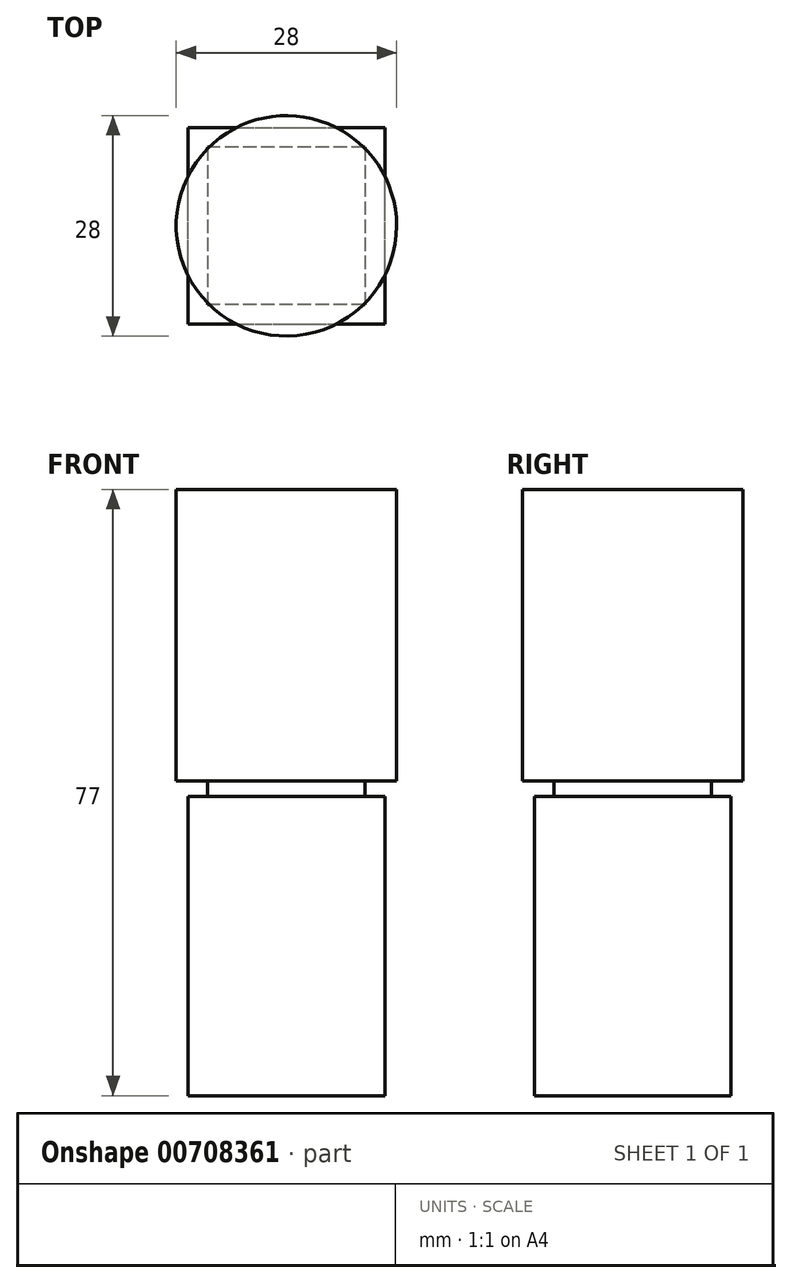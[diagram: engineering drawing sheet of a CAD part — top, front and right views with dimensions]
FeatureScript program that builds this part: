
annotation { "Feature Type Name" : "Feature", "Feature Type Description" : "" }
export const myFeature = defineFeature(function(context is Context, id is Id, definition is map)
    precondition{}
    {
        {
            var Q0;
            Q0=qCreatedBy(makeId("Top.planeOp"),FACE);
            var sketch = newSketch(context, id + "F0", { "sketchPlane" : qUnion([Q0])});
            skLineSegment(sketch, "E0.bottom", {"start": v(0, 0) * mm, "end": v(25, 0) * mm});
            skLineSegment(sketch, "E0.top", {"start": v(0, 25) * mm, "end": v(25, 25) * mm});
            skLineSegment(sketch, "E0.left", {"start": v(0, 0) * mm, "end": v(0, 25) * mm});
            skLineSegment(sketch, "E0.right", {"start": v(25, 0) * mm, "end": v(25, 25) * mm});
            skSolve(sketch);
        }
        {
            var Q0;
            Q0=makeQuery(id+"F0.imprint","IMPRINT",FACE,{"disambiguationData":[TD([[makeQuery(id+"F0.imprint","IMPRINT",EDGE,{"derivedFrom":sQuery(id+"F0.wireOp",EDGE,"E0.bottom")}),1.0]])]});
            extrude(context, id + "F1", {"entities" : qUnion([Q0]), "depth" : 38 * mm, "offsetDistance" : 25 * mm});
        }
        {
            var Q0;
            Q0=makeQuery(id+"F1.opExtrude","CAP_FACE",FACE,{"disambiguationData":[OSD([sQuery(id+"F0.wireOp",EDGE,"E0.bottom"),sQuery(id+"F0.wireOp",EDGE,"E0.top"),sQuery(id+"F0.wireOp",EDGE,"E0.left"),sQuery(id+"F0.wireOp",EDGE,"E0.right")])],"isStart":false});
            var sketch = newSketch(context, id + "F2", { "sketchPlane" : qUnion([Q0])});
            skPoint(sketch, "E1.centerSnap0", {"position": v(0, 12.5) * mm});
            skPoint(sketch, "E1.centerSnap1", {"position": v(12.5, 0) * mm});
            skLineSegment(sketch, "E2.bottom", {"start": v(22.5, 22.5) * mm, "end": v(2.5, 22.5) * mm});
            skLineSegment(sketch, "E2.top", {"start": v(22.5, 2.5) * mm, "end": v(2.5, 2.5) * mm});
            skLineSegment(sketch, "E2.left", {"start": v(22.5, 22.5) * mm, "end": v(22.5, 2.5) * mm});
            skLineSegment(sketch, "E2.right", {"start": v(2.5, 22.5) * mm, "end": v(2.5, 2.5) * mm});
            skPoint(sketch, "E2.middle", {"position": v(12.5, 12.5) * mm});
            skSolve(sketch);
        }
        {
            var Q0;
            Q0=makeQuery(id+"F2.imprint","IMPRINT",FACE,{"disambiguationData":[TD([[makeQuery(id+"F2.imprint","IMPRINT",EDGE,{"derivedFrom":sQuery(id+"F2.wireOp",EDGE,"E2.bottom")}),1.0]])]});
            extrude(context, id + "F3", {"entities" : qUnion([Q0]), "operationType" : NewBodyOperationType.ADD, "depth" : 2 * mm, "offsetDistance" : 25 * mm});
        }
        {
            var Q0;
            Q0=makeQuery(id+"F3.opExtrude","CAP_FACE",FACE,{"disambiguationData":[OSD([sQuery(id+"F2.wireOp",EDGE,"E2.bottom"),sQuery(id+"F2.wireOp",EDGE,"E2.top"),sQuery(id+"F2.wireOp",EDGE,"E2.left"),sQuery(id+"F2.wireOp",EDGE,"E2.right")])],"isStart":false});
            var sketch = newSketch(context, id + "F4", { "sketchPlane" : qUnion([Q0])});
            skCircle(sketch, "E3", {"center": v(12.5, 12.5) * mm, "radius": 14 * mm});
            skPoint(sketch, "E3.centerSnap0", {"position": v(2.5, 12.5) * mm});
            skPoint(sketch, "E3.centerSnap1", {"position": v(12.5, 2.5) * mm});
            skSolve(sketch);
        }
        {
            var Q0;
            {var subQ0=sQuery(id+"F4.wireOp",EDGE,"E3");var subQ1=makeQuery(id+"F3.opExtrude","CAP_EDGE",EDGE,{"disambiguationData":[OSD([sQuery(id+"F2.wireOp",EDGE,"E2.bottom")])],"isStart":false});var subQ2=makeQuery(id+"F4.imprint","INTERSECT",VERTEX,{"disambiguationData":[OD(0.0)],"derivedFrom":[subQ1,subQ0]});Q0=makeQuery(id+"F4.imprint","IMPRINT",FACE,{"disambiguationData":[TD([[makeQuery(id+"F4.imprint","IMPRINT",EDGE,{"disambiguationData":[TD([[subQ2,-1.0]])],"derivedFrom":subQ0}),1.0]])]});}
            var Q1;
            {var subQ0=sQuery(id+"F4.wireOp",EDGE,"E3");var subQ8=makeQuery(id+"F3.opExtrude","CAP_EDGE",EDGE,{"disambiguationData":[OSD([sQuery(id+"F2.wireOp",EDGE,"E2.bottom")])],"isStart":false});var subQ11=makeQuery(id+"F4.imprint","INTERSECT",VERTEX,{"disambiguationData":[OD(0.0)],"derivedFrom":[subQ8,subQ0]});Q1=makeQuery(id+"F4.imprint","IMPRINT",FACE,{"disambiguationData":[TD([[makeQuery(id+"F4.imprint","IMPRINT",EDGE,{"disambiguationData":[TD([[subQ11,1.0]])],"derivedFrom":subQ0}),1.0]])]});}
            var Q2;
            {var subQ0=sQuery(id+"F4.wireOp",EDGE,"E3");var subQ1=makeQuery(id+"F3.opExtrude","CAP_EDGE",EDGE,{"disambiguationData":[OSD([sQuery(id+"F2.wireOp",EDGE,"E2.right")])],"isStart":false});var subQ2=makeQuery(id+"F4.imprint","INTERSECT",VERTEX,{"disambiguationData":[OD(0.0)],"derivedFrom":[subQ1,subQ0]});Q2=makeQuery(id+"F4.imprint","IMPRINT",FACE,{"disambiguationData":[TD([[makeQuery(id+"F4.imprint","IMPRINT",EDGE,{"disambiguationData":[TD([[subQ2,-1.0]])],"derivedFrom":subQ0}),1.0]])]});}
            var Q3;
            {var subQ0=sQuery(id+"F4.wireOp",EDGE,"E3");var subQ1=makeQuery(id+"F3.opExtrude","CAP_EDGE",EDGE,{"disambiguationData":[OSD([sQuery(id+"F2.wireOp",EDGE,"E2.top")])],"isStart":false});var subQ2=makeQuery(id+"F4.imprint","INTERSECT",VERTEX,{"disambiguationData":[OD(0.0)],"derivedFrom":[subQ1,subQ0]});Q3=makeQuery(id+"F4.imprint","IMPRINT",FACE,{"disambiguationData":[TD([[makeQuery(id+"F4.imprint","IMPRINT",EDGE,{"disambiguationData":[TD([[subQ2,-1.0]])],"derivedFrom":subQ0}),1.0]])]});}
            var Q4;
            {var subQ0=sQuery(id+"F4.wireOp",EDGE,"E3");var subQ1=makeQuery(id+"F3.opExtrude","CAP_EDGE",EDGE,{"disambiguationData":[OSD([sQuery(id+"F2.wireOp",EDGE,"E2.left")])],"isStart":false});var subQ2=makeQuery(id+"F4.imprint","INTERSECT",VERTEX,{"disambiguationData":[OD(0.0)],"derivedFrom":[subQ1,subQ0]});Q4=makeQuery(id+"F4.imprint","IMPRINT",FACE,{"disambiguationData":[TD([[makeQuery(id+"F4.imprint","IMPRINT",EDGE,{"disambiguationData":[TD([[subQ2,1.0]])],"derivedFrom":subQ0}),1.0]])]});}
            extrude(context, id + "F5", {"entities" : qUnion([Q0, Q1, Q2, Q3, Q4]), "operationType" : NewBodyOperationType.ADD, "depth" : 37 * mm, "offsetDistance" : 25 * mm});
        }
    });
